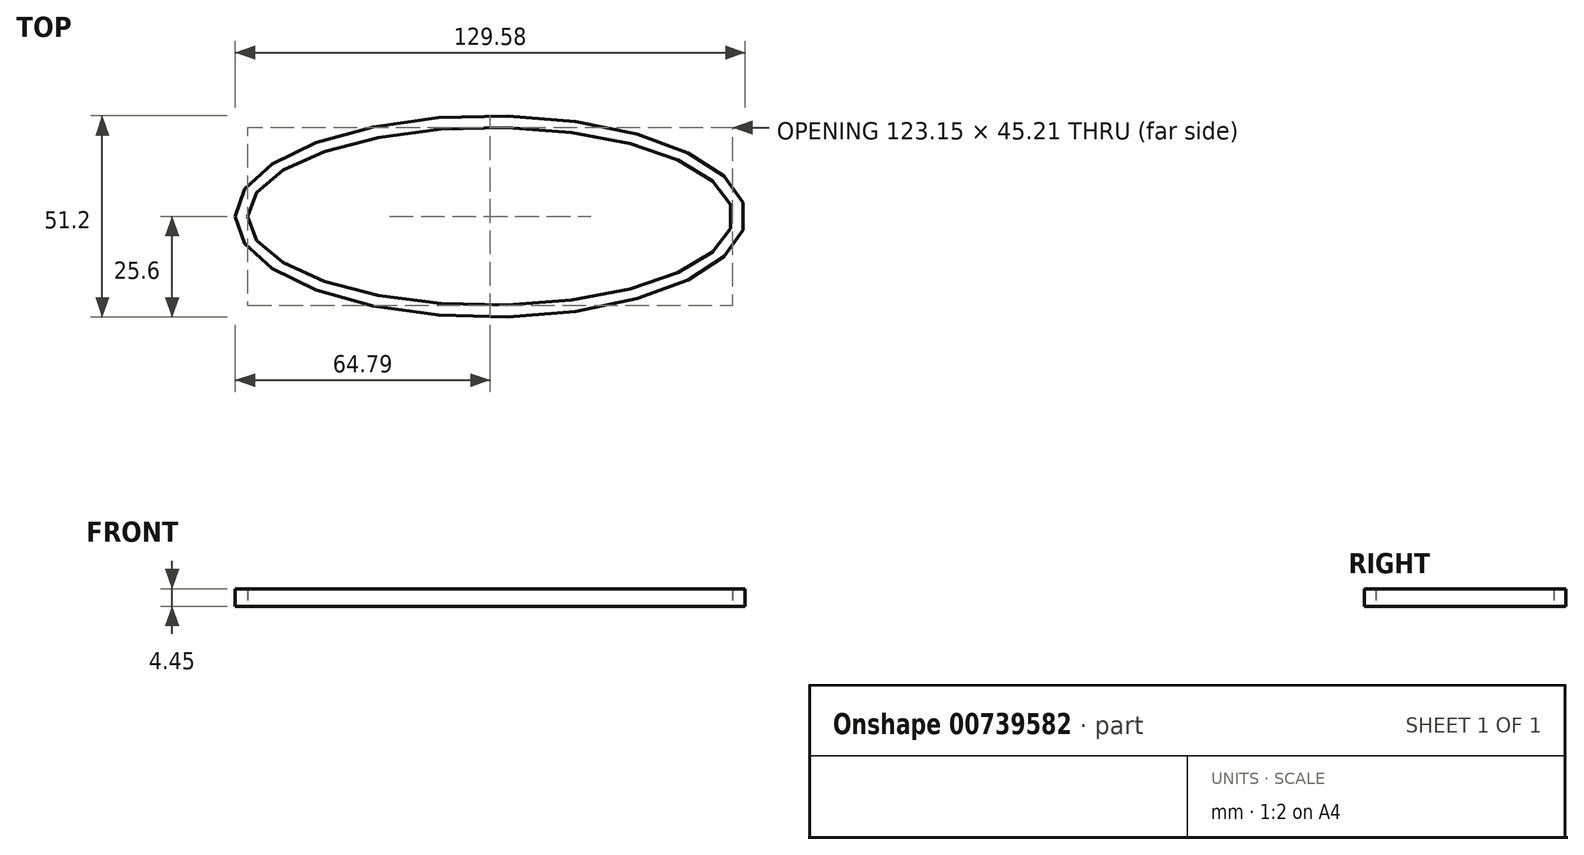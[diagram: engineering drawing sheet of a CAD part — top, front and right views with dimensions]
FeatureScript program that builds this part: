
annotation { "Feature Type Name" : "Feature", "Feature Type Description" : "" }
export const myFeature = defineFeature(function(context is Context, id is Id, definition is map)
    precondition{}
    {
        {
            var Q0;
            Q0=qCreatedBy(makeId("Top.planeOp"),FACE);
            var sketch = newSketch(context, id + "F0", { "sketchPlane" : qUnion([Q0])});
            skEllipse(sketch, "E0", {"center": v(0, 0) * mm, "majorRadius": 64.79 * mm, "minorRadius": 25.6 * mm, "majorAxis": v(-1, 0)});
            skEllipse(sketch, "E1", {"center": v(0, 0) * mm, "majorRadius": 61.58 * mm, "minorRadius": 22.6 * mm, "majorAxis": v(-1, 0)});
            skSolve(sketch);
        }
        {
            var Q0;
            Q0=makeQuery(id+"F0.imprint","IMPRINT",FACE,{"disambiguationData":[TD([[makeQuery(id+"F0.imprint","IMPRINT",EDGE,{"derivedFrom":sQuery(id+"F0.wireOp",EDGE,"E0")}),1.0]])]});
            extrude(context, id + "F1", {"entities" : qUnion([Q0]), "depth" : 4.44 * mm, "offsetDistance" : 25.4 * mm});
        }
    });
